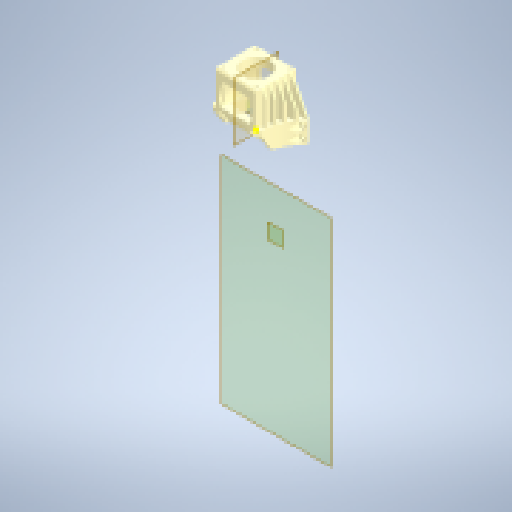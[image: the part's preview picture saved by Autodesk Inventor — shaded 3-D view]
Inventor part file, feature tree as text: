
AUTODESK INVENTOR PART (.ipt)
format: ipt  version: 2025.2 (Build 292293000, 293)  size: 622,080 bytes
history: native  units: mm
features: extrude x17, reference x16, other x5, plane x4, mirror x4, projected_geometry x4, chamfer x3, pattern_linear x1, fillet x1, sketch x1
ambient origin geometry x8: Origin, YZ Plane, XZ Plane, XY Plane, X Axis, Y Axis, Z Axis, Center Point
bodies: Solid1 (feature_tree)
feature tree (56):
  extrude  "Extrusion1"  Depth=38.6mm
  extrude  "Extrusion2"  Depth=47.14mm
  extrude  "Extrusion3"  Depth=4.2mm
  extrude  "Extrusion4"  Depth=7.5mm TaperAngle=0.0deg
  extrude  "Extrusion5"  Depth=2.0mm
  extrude  "Extrusion6"  Depth=5.0mm
  extrude  "Extrusion7"  Depth=5.0mm
  plane  "Work Plane1"
  mirror  "Mirror1"
  extrude  "Extrusion8"  Depth=38.0mm
  extrude  "Extrusion9"  Depth=7.5mm TaperAngle=0.0deg
  extrude  "Extrusion10"  Depth=10.0mm TaperAngle=0.0deg
  extrude  "Extrusion11"  Depth=0.5mm
  plane  "Work Plane2"
  extrude  "Extrusion12"  Depth=5.0mm
  mirror  "Mirror2"
  extrude  "Extrusion13"  Depth=2.0mm
  pattern_linear  "Rectangular Pattern1"  Spacing1=1.0mm  [1 undecoded]
  mirror  "Mirror3"
  extrude  "Extrusion14"  Depth=1.0mm
  mirror  "Mirror4"
  chamfer  "Chamfer1"  Distance=1.0mm
  fillet  "Fillet1"  [1 undecoded]
  plane  "Work Plane4"
  plane  "Work Plane5"
  extrude  "Extrusion15"  Depth=5.0mm
  chamfer  "Chamfer2"  Distance=5.0mm
  extrude  "Extrusion16"  Depth=4.35mm TaperAngle=0.0deg
  extrude  "Extrusion17"  Depth=10.1mm TaperAngle=0.0deg
  chamfer  "Chamfer3"  Distance=0.15mm
  projected_geometry  "Projected Loop1"
  reference  "Reference1"
  reference  "Reference2"
  reference  "Reference3"
  reference  "Reference4"
  reference  "Reference5"
  reference  "Reference6"
  reference  "Reference7"
  projected_geometry  "Projected Loop2"
  projected_geometry  "Projected Loop3"
  projected_geometry  "Projected Loop4"
  reference  "Reference8"
  reference  "Reference9"
  reference  "Reference10"
  reference  "Reference11"
  reference  "Reference12"
  reference  "Reference13"
  reference  "Reference14"
  reference  "Reference15"
  reference  "Reference16"
  sketch  "Sketch21"  dims[d2=58.4mm d3=38.6mm d4=47.14mm d5=4.2mm d6=7.5mm d7=0.0mm d9=2.0mm d10=5.0mm d12=5.0mm d13=38.0mm d14=7.5mm d15=0.0mm d16=10.0mm d17=0.0mm d18=0.5mm d19=5.0mm d20=2.0mm d21=1.0mm d22=1.0mm d23=1.0mm d24=0.0mm d25=5.0mm d26=5.0mm d27=4.35mm d28=0.0mm d29=10.1mm d30=0.0mm d31=0.15mm d32=2.5mm d33=10.1mm d34=0.0mm d35=4.0mm d36=0.0mm d37=0.3mm d38=0.3mm d39=0.3mm d40=30.0mm d41=0.0mm d42=20.0mm d43=5.0mm d44=14.75mm d45=0.0mm d46=217.5mm d47=0.0mm d48=5.7625mm d50=5.5mm d51=15.0mm d52=217.5mm d53=0.0mm d54=-5.0mm d55=11.0mm d56=217.5mm d57=0.0mm d58=3.0mm d59=0.0mm d60=50.0mm d62=10.0mm d63=10.0mm d64=0.0mm d65=2.0mm d66=2.0mm d67=45.0deg d68=2.0mm d69=10.0mm d70=5.0mm d71=0.0mm d72=2.0mm d73=2.0mm d74=45.0deg d75=37.0mm d76=0.0mm d78=0.2mm d79=37.0mm d80=0.0mm d81=2.0mm d82=2.0mm d83=45.0deg]
  parser-record x1  (decoder bookkeeping rows leaked as tree rows — omitted from the tree; the rows remain in map.json)
  other  "Z_GANTRY.iam"
  other  "Z_Gantry_Plate_Spaced:1"
  other  "Z_Gantry_Plate:1"
  other  "BK10:1"
note: 2 required parameter values undecoded (feature->parameter linkage not recoverable at this tier; creation-order binding heuristic only, values carry confidence <= 0.55)
note: 1 file-system path scrubbed to <path> (originals preserved in map.json)
